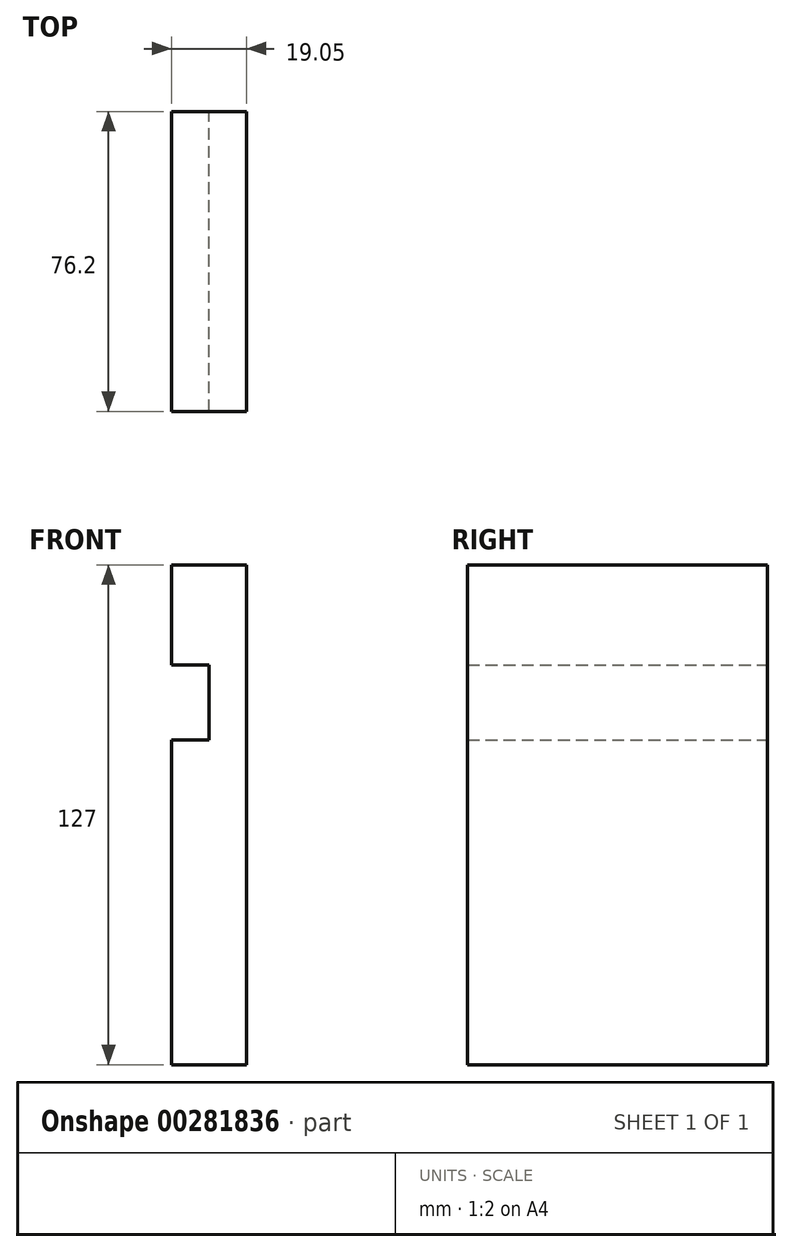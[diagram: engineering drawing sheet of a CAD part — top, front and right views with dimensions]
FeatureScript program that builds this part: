
annotation { "Feature Type Name" : "Feature", "Feature Type Description" : "" }
export const myFeature = defineFeature(function(context is Context, id is Id, definition is map)
    precondition{}
    {
        {
            var Q0;
            Q0=qCreatedBy(makeId("Front.planeOp"),FACE);
            var sketch = newSketch(context, id + "F0", { "sketchPlane" : qUnion([Q0])});
            skLineSegment(sketch, "E0", {"start": v(-30.93, 72.37) * mm, "end": v(-30.93, 46.97) * mm});
            skLineSegment(sketch, "E1", {"start": v(-30.93, 46.97) * mm, "end": v(-21.4, 46.97) * mm});
            skLineSegment(sketch, "E2", {"start": v(-21.4, 46.97) * mm, "end": v(-21.4, 27.92) * mm});
            skLineSegment(sketch, "E3", {"start": v(-21.4, 27.92) * mm, "end": v(-30.93, 27.92) * mm});
            skLineSegment(sketch, "E4", {"start": v(-30.93, 72.37) * mm, "end": v(-11.88, 72.37) * mm});
            skLineSegment(sketch, "E5", {"start": v(-11.88, 72.37) * mm, "end": v(-11.88, -54.63) * mm});
            skLineSegment(sketch, "E6", {"start": v(-11.88, -54.63) * mm, "end": v(-30.93, -54.63) * mm});
            skLineSegment(sketch, "E7", {"start": v(-30.93, -54.63) * mm, "end": v(-30.93, 27.92) * mm});
            skSolve(sketch);
        }
        {
            var Q0;
            Q0 = qSketchRegion(id + "F0", true);
            extrude(context, id + "F1", {"entities" : qUnion([Q0]), "depth" : 76.2 * mm});
        }
    });
